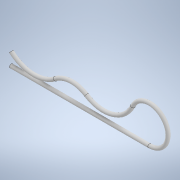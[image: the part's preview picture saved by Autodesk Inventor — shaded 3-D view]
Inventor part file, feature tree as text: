
AUTODESK INVENTOR PART (.ipt)
format: ipt  version: 2022 (Build 260153000, 153)  size: 140,800 bytes
history: native  units: mm
features: sketch x2, sweep x1
ambient origin geometry x8: Origin, YZ Plane, XZ Plane, XY Plane, X Axis, Y Axis, Z Axis, Center Point
bodies: Solid1 (feature_tree)
feature tree (3):
  sweep  "Sweep1"
  sketch  "Sketch2"  dims[d2=2.0mm d3=90.0deg]
  sketch  "Sketch3"  dims[d4=75.0mm d6=2.0mm d7=0.0mm d8=0.0mm d9=10.0mm d10=4.0mm]
